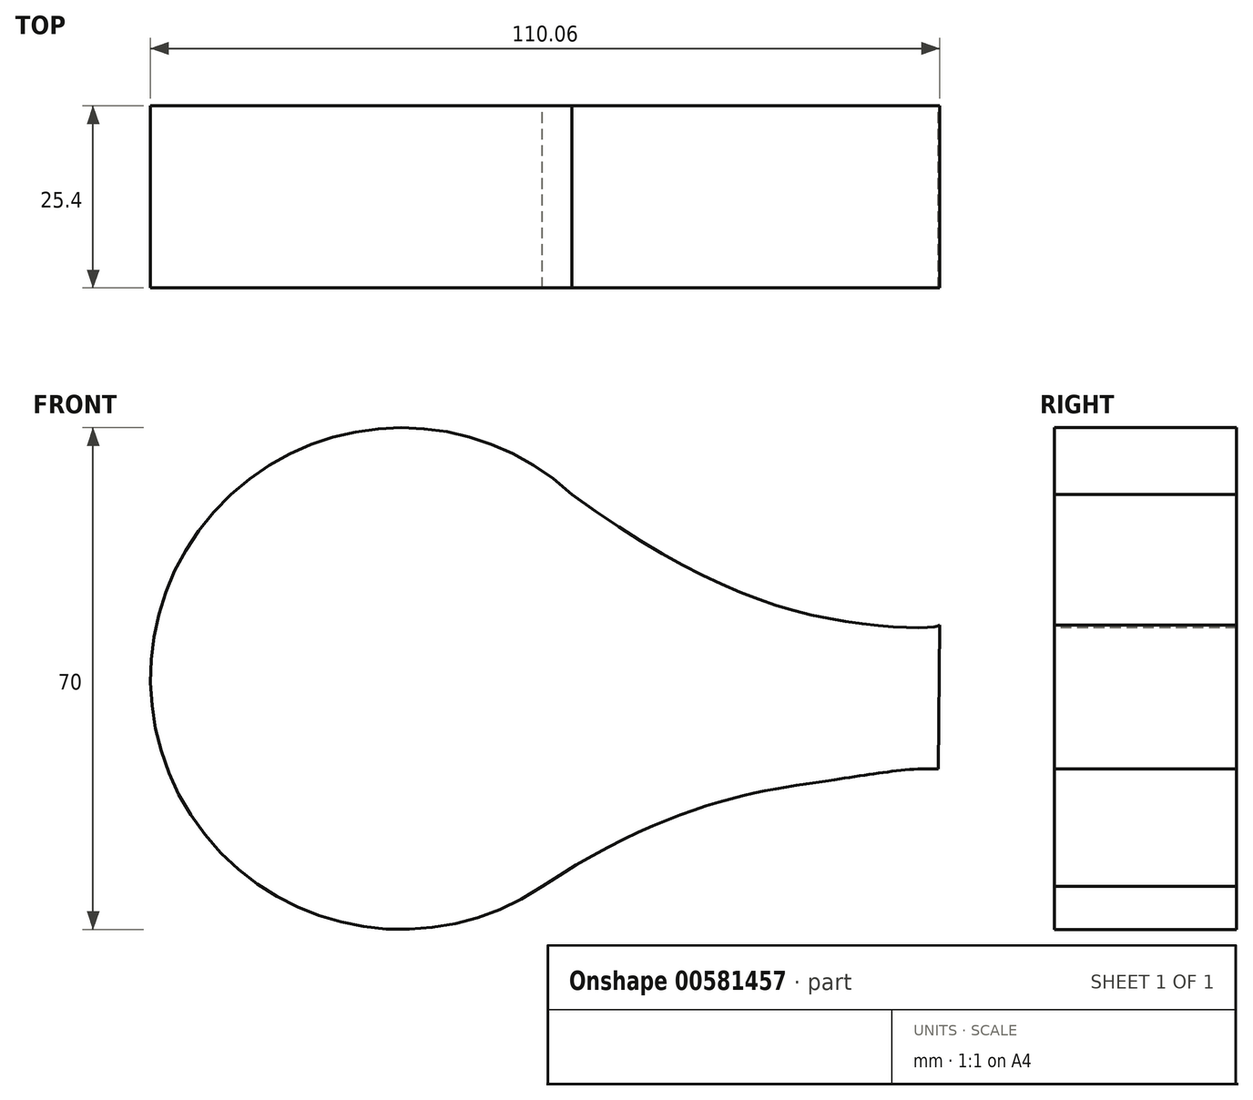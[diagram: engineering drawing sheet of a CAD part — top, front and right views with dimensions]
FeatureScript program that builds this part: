
annotation { "Feature Type Name" : "Feature", "Feature Type Description" : "" }
export const myFeature = defineFeature(function(context is Context, id is Id, definition is map)
    precondition{}
    {
        {
            var Q0;
            Q0=qCreatedBy(makeId("Front.planeOp"),FACE);
            var sketch = newSketch(context, id + "F0", { "sketchPlane" : qUnion([Q0])});
            skCircle(sketch, "E0", {"center": v(-36.3, 5.07) * mm, "radius": 35 * mm});
            skFitSpline(sketch, "E1", {"points": [v(-18.23, 35.05) * mm, v(24.12, 13.3) * mm, v(38.38, 12.31) * mm, v(38.77, 12.5) * mm], "startDerivative": vector(89.91, -69.73) * mm, "endDerivative": vector(4.18, 3.4) * mm});
            skFitSpline(sketch, "E2", {"points": [v(-17.44, -24.42) * mm, v(24.11, -9.04) * mm, v(38.77, -7.56) * mm], "startDerivative": vector(90.45, 60) * mm, "endDerivative": vector(35.2, -1.96) * mm});
            skFitSpline(sketch, "E3", {"points": [v(38.58, -8.08) * mm, v(38.77, 12.5) * mm], "startDerivative": vector(0.2, 21.5) * mm, "endDerivative": vector(0.2, 21.5) * mm});
            skLineSegment(sketch, "E4", {"start": v(24.11, 13.23) * mm, "end": v(24.11, -9.04) * mm});
            skSolve(sketch);
        }
        {
            var Q0;
            Q0 = qSketchRegion(id + "F0", true);
            extrude(context, id + "F1", {"entities" : qUnion([Q0]), "depth" : 25.4 * mm, "offsetDistance" : 25.4 * mm});
        }
    });
